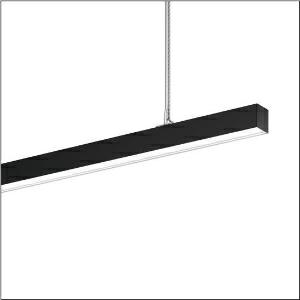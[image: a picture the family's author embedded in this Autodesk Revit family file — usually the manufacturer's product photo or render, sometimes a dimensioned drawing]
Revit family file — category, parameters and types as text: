
# Revit family: silica_r__21_51mx33tbt9b_b685
name_source: partatom
category: Lighting Fixtures
units: mm (PartAtom-declared; Revit-internal decimal feet)

## family parameters
Cut with Voids When Loaded = No
Host = Face
Light Source = No
Part Type = Normal
Room Calculation Point = No
Round Connector Dimension = Use Diameter
Shared = No

## types (1)
- --- (1 x LED, 7170 lm, 67.4 W, 6500K)
    Apparent Load = 67 VA
    CIE Flux Codes = 78 96 99 56 100
    Color Rendering = 80
    Color Temperature = 6500K
    Default Elevation = 1800 mm
    Description = Silica® 21, office luminaire, primary optical cover: prismatic diffuser, of PMMA, CAT 2 (L<= 3000cd/m²), light emission: direct/indirect distribution, primary light characteristic: symmetric, installation type: suspended mounting, LED, rated luminous flux: 7.170lm, luminous efficacy: 101lm/W, light colour: 8tw, colour temperature: 2700..6500K, control gear: ECG DALI, with terminal, 3+2-pole, max. 2.5mm², mains connection: 220..240V, AC, 50/60Hz, rated input power: 70.8W, luminaire housing, of aluminium, jet black (RAL 9005), length: 1.504mm, width: 53mm, height: 53mm, protection rating (complete): IP20, insulation class (complete): insulation class I (protective earthing), certification: CE, permissible operating ambient temperature: 0..+35°C, standard: EN 50419, packaging unit: 1 piece
    Height = 53 mm
    Lamp = 1 x LED
    Lamp Light Flux = 7170 lm
    Lamp Power = 67.4 W
    Lamp count = 1
    Length = 1504 mm
    Luminous efficacy = 106 lm/W
    Manufacturer = Siteco
    ModVariant = No
    Model = 51MX33TBT9B
    Mounting Place = Ceiling
    Mounting Type = Pendant
    Number of Poles = 1
    OnlyDefault = Yes
    Power Factor = 1
    Product Name = Silica® 21
    Product group = office luminaire | ceiling pendant
    ProductGroupID = 902
    Protection Class = Protection class I
    Protection Degree = IP 20
    RLX_Detail_Level = 1
    RLX_Emergency_Light_Flux = 0 lm
    RLX_Emergency_Type = 0
    RLX_Emergency_Type_DB = No
    RlxData = <blob elided: 22921 chars, md5=a76355e8>
    Socket = socket
    Standby Power = 0 W
    System Light Flux = 7170 lm
    System Power = 67 W
    Type Comments = individual setting
    Type Image = l_1335856.jpg
    URL = http://relux.com
    VarID = @adj_109561
    Voltage = 0 V
    Weight = 0.00 kg
    Width = 53 mm

## geometry (parser evidence)
native form markers: Blend x4, Sweep x14
no freeform markers — native parametric forms only
